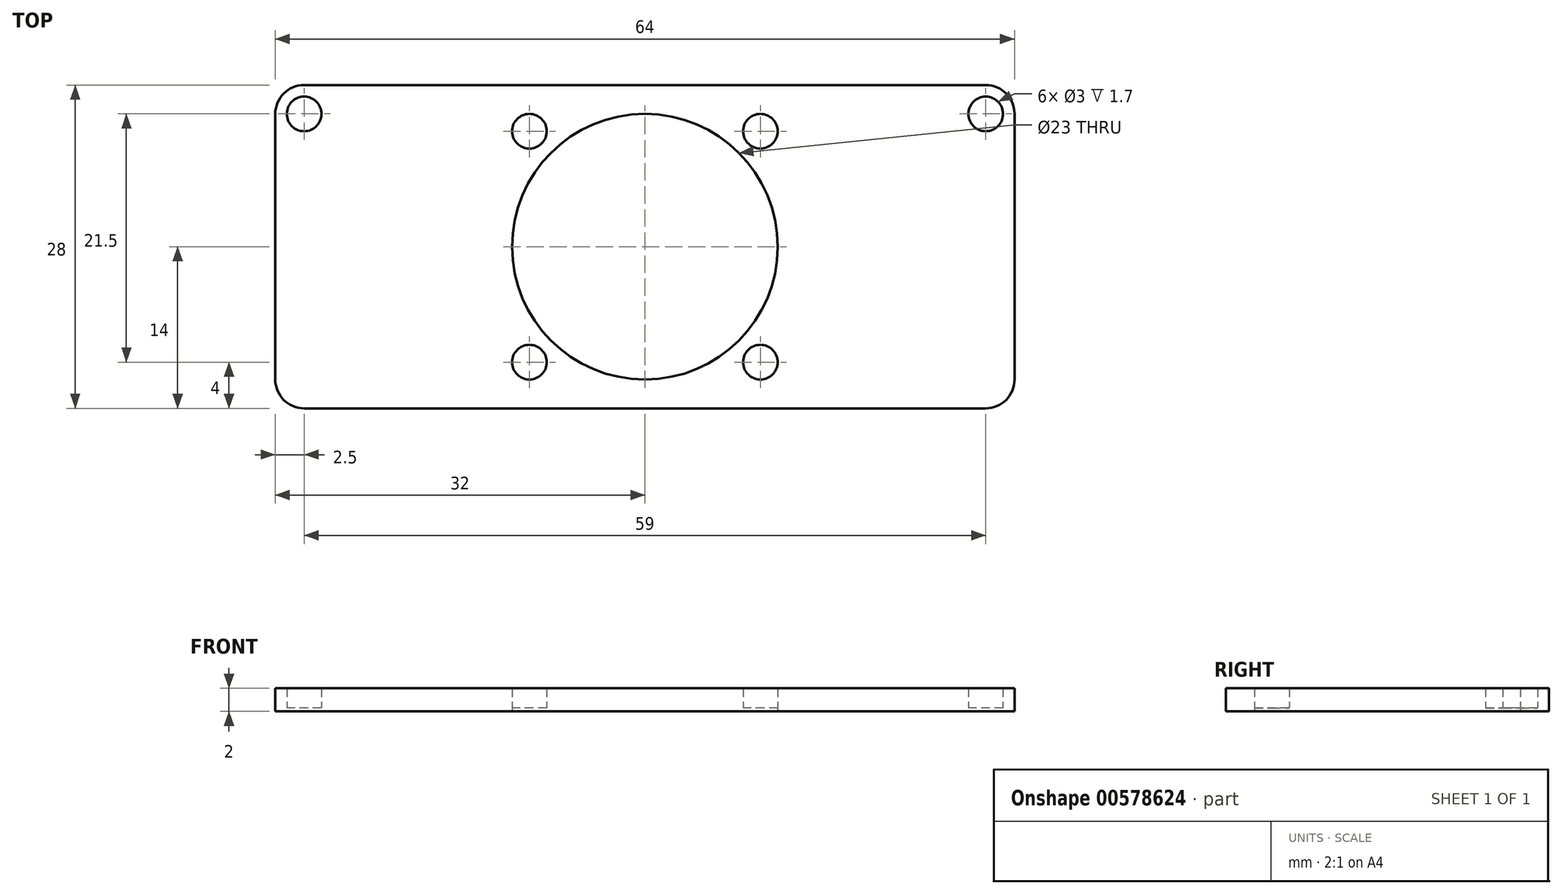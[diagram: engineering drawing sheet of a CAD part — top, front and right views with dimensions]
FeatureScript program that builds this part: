
annotation { "Feature Type Name" : "Feature", "Feature Type Description" : "" }
export const myFeature = defineFeature(function(context is Context, id is Id, definition is map)
    precondition{}
    {
        {
            var Q0;
            Q0=qCreatedBy(makeId("Top.planeOp"),FACE);
            var sketch = newSketch(context, id + "F0", { "sketchPlane" : qUnion([Q0])});
            skLineSegment(sketch, "E0.bottom", {"start": v(29.5, 14) * mm, "end": v(-29.5, 14) * mm});
            skLineSegment(sketch, "E0.top", {"start": v(29.5, -14) * mm, "end": v(-29.5, -14) * mm});
            skLineSegment(sketch, "E0.left", {"start": v(32, 11.5) * mm, "end": v(32, -11.5) * mm});
            skLineSegment(sketch, "E0.right", {"start": v(-32, 11.5) * mm, "end": v(-32, -11.5) * mm});
            skPoint(sketch, "E0.middle", {"position": v(0, 0) * mm});
            skCircle(sketch, "E1", {"center": v(-29.5, 11.5) * mm, "radius": 1.5 * mm});
            skCircle(sketch, "E2", {"center": v(29.5, 11.5) * mm, "radius": 1.5 * mm});
            skCircle(sketch, "E3", {"center": v(0, 0) * mm, "radius": 11.5 * mm});
            skPoint(sketch, "E4.visualSharp", {"position": v(-32, 14) * mm});
            skArc(sketch, "E4.filletArc", {"start": v(-29.5, 14) * mm, "mid": v(-31.27, 13.27) * mm, "end": v(-32, 11.5) * mm});
            skPoint(sketch, "E5.visualSharp", {"position": v(32, 14) * mm});
            skArc(sketch, "E5.filletArc", {"start": v(32, 11.5) * mm, "mid": v(31.27, 13.27) * mm, "end": v(29.5, 14) * mm});
            skPoint(sketch, "E6.visualSharp", {"position": v(32, -14) * mm});
            skArc(sketch, "E6.filletArc", {"start": v(29.5, -14) * mm, "mid": v(31.27, -13.27) * mm, "end": v(32, -11.5) * mm});
            skPoint(sketch, "E7.visualSharp", {"position": v(-32, -14) * mm});
            skArc(sketch, "E7.filletArc", {"start": v(-32, -11.5) * mm, "mid": v(-31.27, -13.27) * mm, "end": v(-29.5, -14) * mm});
            skLineSegment(sketch, "E8", {"start": v(-29.5, 11.5) * mm, "end": v(-29.5, 14) * mm, "construction": true});
            skLineSegment(sketch, "E9", {"start": v(-29.5, 11.5) * mm, "end": v(-32, 11.5) * mm, "construction": true});
            skLineSegment(sketch, "E10", {"start": v(29.5, 11.5) * mm, "end": v(29.5, 14) * mm, "construction": true});
            skLineSegment(sketch, "E11", {"start": v(29.5, 11.5) * mm, "end": v(32, 11.5) * mm, "construction": true});
            skLineSegment(sketch, "E12", {"start": v(-29.5, 11.5) * mm, "end": v(-29.5, 13) * mm, "construction": true});
            skLineSegment(sketch, "E13", {"start": v(-29.5, 11.5) * mm, "end": v(-31, 11.5) * mm, "construction": true});
            skLineSegment(sketch, "E14", {"start": v(0, 0) * mm, "end": v(0, 11.5) * mm, "construction": true});
            skLineSegment(sketch, "E15", {"start": v(0, 0) * mm, "end": v(-10, 10) * mm, "construction": true});
            skCircle(sketch, "E16", {"center": v(-10, 10) * mm, "radius": 1.5 * mm});
            skCircle(sketch, "E17.1.0", {"center": v(-10, -10) * mm, "radius": 1.5 * mm});
            skCircle(sketch, "E17.2.0", {"center": v(10, -10) * mm, "radius": 1.5 * mm});
            skCircle(sketch, "E18.1.3.0", {"center": v(10, 10) * mm, "radius": 1.5 * mm});
            skSolve(sketch);
        }
        {
            var Q0;
            Q0=makeQuery(id+"F0.imprint","IMPRINT",FACE,{"disambiguationData":[TD([[makeQuery(id+"F0.imprint","IMPRINT",EDGE,{"derivedFrom":sQuery(id+"F0.wireOp",EDGE,"E0.bottom")}),1.0]])]});
            extrude(context, id + "F1", {"entities" : qUnion([Q0]), "depth" : 2 * mm, "offsetDistance" : 25 * mm});
        }
        {
            var Q0;
            Q0=makeQuery(id+"F0.imprint","IMPRINT",FACE,{"disambiguationData":[TD([[makeQuery(id+"F0.imprint","IMPRINT",EDGE,{"derivedFrom":sQuery(id+"F0.wireOp",EDGE,"E1")}),1.0]])]});
            var Q1;
            Q1=makeQuery(id+"F0.imprint","IMPRINT",FACE,{"disambiguationData":[TD([[makeQuery(id+"F0.imprint","IMPRINT",EDGE,{"derivedFrom":sQuery(id+"F0.wireOp",EDGE,"E16")}),1.0]])]});
            var Q2;
            Q2=makeQuery(id+"F0.imprint","IMPRINT",FACE,{"disambiguationData":[TD([[makeQuery(id+"F0.imprint","IMPRINT",EDGE,{"derivedFrom":sQuery(id+"F0.wireOp",EDGE,"E18.1.3.0")}),1.0]])]});
            var Q3;
            Q3=makeQuery(id+"F0.imprint","IMPRINT",FACE,{"disambiguationData":[TD([[makeQuery(id+"F0.imprint","IMPRINT",EDGE,{"derivedFrom":sQuery(id+"F0.wireOp",EDGE,"E2")}),1.0]])]});
            var Q4;
            Q4=makeQuery(id+"F0.imprint","IMPRINT",FACE,{"disambiguationData":[TD([[makeQuery(id+"F0.imprint","IMPRINT",EDGE,{"derivedFrom":sQuery(id+"F0.wireOp",EDGE,"E17.2.0")}),1.0]])]});
            var Q5;
            Q5=makeQuery(id+"F0.imprint","IMPRINT",FACE,{"disambiguationData":[TD([[makeQuery(id+"F0.imprint","IMPRINT",EDGE,{"derivedFrom":sQuery(id+"F0.wireOp",EDGE,"E17.1.0")}),1.0]])]});
            extrude(context, id + "F2", {"entities" : qUnion([Q0, Q1, Q2, Q3, Q4, Q5]), "operationType" : NewBodyOperationType.ADD, "depth" : 0.3 * mm, "offsetDistance" : 25 * mm});
        }
    });
